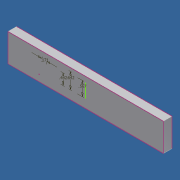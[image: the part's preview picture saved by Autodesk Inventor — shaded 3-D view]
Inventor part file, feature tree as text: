
AUTODESK INVENTOR PART (.ipt)
format: ipt  version: unknown  size: 174,080 bytes
history: native  units: in
note: dims shown in document units (in); Inventor stores cm internally (conversion verified against a paired STEP export)
features: sketch x3, extrude x1
ambient origin geometry x8: Origin, YZ Plane, XZ Plane, XY Plane, X Axis, Y Axis, Z Axis, Center Point
bodies: Solid1 (feature_tree)
feature tree (4):
  extrude  "Extrusion1"  Depth=1.125in
  sketch  "Sketch2"  dims[d2=0.35in d3=0.0in]
  sketch  "Sketch3"  dims[d6=0.567in d8=0.442in d9=0.642in d10=0.171in]
  sketch  "Sketch1"  dims[d0=6.26in d1=1.125in]
